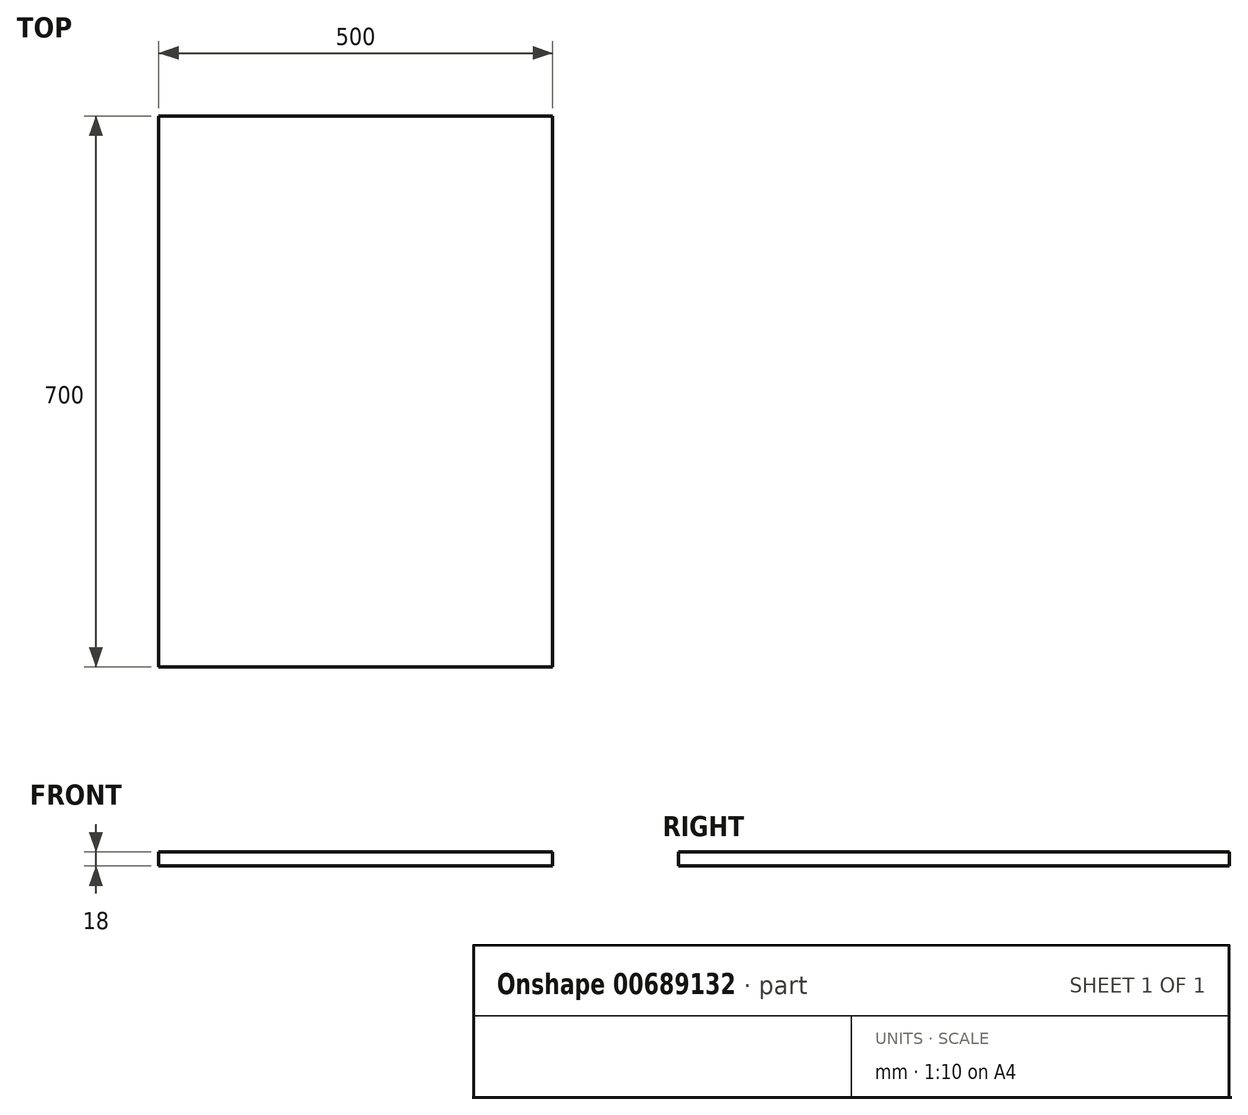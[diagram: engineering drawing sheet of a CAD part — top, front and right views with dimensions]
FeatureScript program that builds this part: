
annotation { "Feature Type Name" : "Feature", "Feature Type Description" : "" }
export const myFeature = defineFeature(function(context is Context, id is Id, definition is map)
    precondition{}
    {
        {
            var Q0;
            Q0=qCreatedBy(makeId("Top.planeOp"),FACE);
            var sketch = newSketch(context, id + "F0", { "sketchPlane" : qUnion([Q0])});
            skLineSegment(sketch, "E0.bottom", {"start": v(0, 0) * mm, "end": v(500, 0) * mm});
            skLineSegment(sketch, "E0.top", {"start": v(0, 700) * mm, "end": v(500, 700) * mm});
            skLineSegment(sketch, "E0.left", {"start": v(0, 0) * mm, "end": v(0, 700) * mm});
            skLineSegment(sketch, "E0.right", {"start": v(500, 0) * mm, "end": v(500, 700) * mm});
            skSolve(sketch);
        }
        {
            var Q0;
            Q0 = qSketchRegion(id + "F0", true);
            extrude(context, id + "F1", {"entities" : qUnion([Q0]), "depth" : 18 * mm, "offsetDistance" : 25 * mm});
        }
    });
